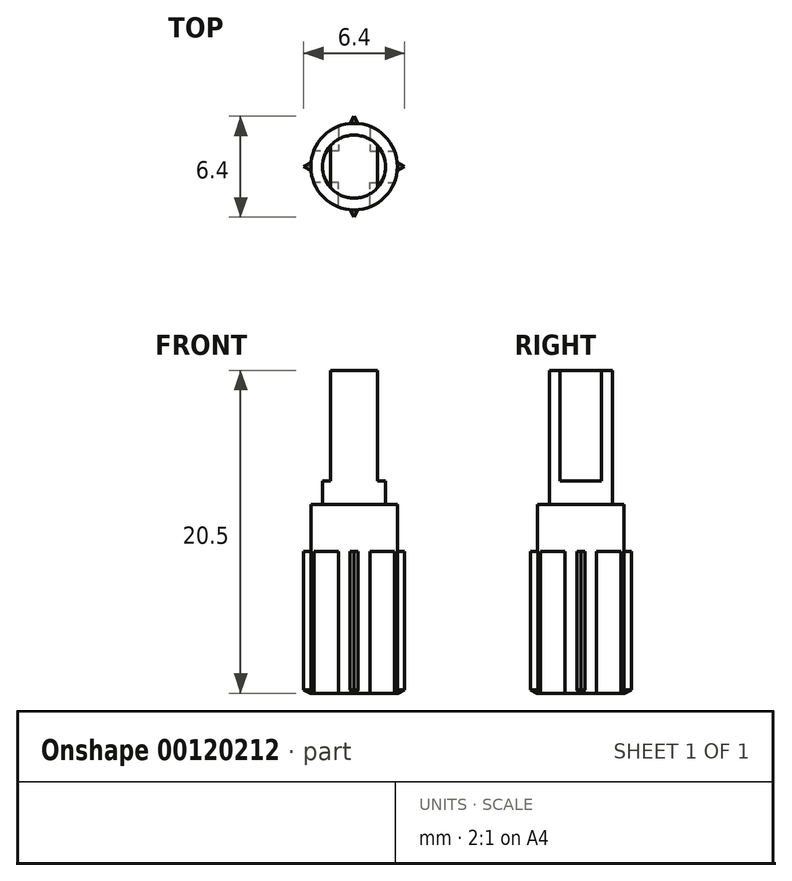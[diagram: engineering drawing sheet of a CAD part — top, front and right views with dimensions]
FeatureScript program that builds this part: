
annotation { "Feature Type Name" : "Feature", "Feature Type Description" : "" }
export const myFeature = defineFeature(function(context is Context, id is Id, definition is map)
    precondition{}
    {
        {
            var Q0;
            Q0=qCreatedBy(makeId("Top.planeOp"),FACE);
            var sketch = newSketch(context, id + "F0", { "sketchPlane" : qUnion([Q0])});
            skCircle(sketch, "E0", {"center": v(0, 0) * mm, "radius": 2.75 * mm});
            skCircle(sketch, "E1", {"center": v(0, 0) * mm, "radius": 2 * mm});
            skSolve(sketch);
        }
        {
            var Q0;
            Q0=makeQuery(id+"F0.imprint","IMPRINT",FACE,{"disambiguationData":[TD([[makeQuery(id+"F0.imprint","IMPRINT",EDGE,{"derivedFrom":sQuery(id+"F0.wireOp",EDGE,"E0")}),1.0]])]});
            var Q1;
            Q1=makeQuery(id+"F0.imprint","IMPRINT",FACE,{"disambiguationData":[TD([[makeQuery(id+"F0.imprint","IMPRINT",EDGE,{"derivedFrom":sQuery(id+"F0.wireOp",EDGE,"E1")}),1.0]])]});
            extrude(context, id + "F1", {"entities" : qUnion([Q0, Q1]), "oppositeDirection" : true, "depth" : 3 * mm});
        }
        {
            var Q0;
            Q0=makeQuery(id+"F0.imprint","IMPRINT",FACE,{"disambiguationData":[TD([[makeQuery(id+"F0.imprint","IMPRINT",EDGE,{"derivedFrom":sQuery(id+"F0.wireOp",EDGE,"E1")}),1.0]])]});
            extrude(context, id + "F2", {"entities" : qUnion([Q0]), "operationType" : NewBodyOperationType.ADD, "depth" : 1.5 * mm});
        }
        {
            var Q0;
            Q0=makeQuery(id+"F2.opExtrude","CAP_FACE",FACE,{"disambiguationData":[OSD([sQuery(id+"F0.wireOp",EDGE,"E1")])],"isStart":false});
            var sketch = newSketch(context, id + "F3", { "sketchPlane" : qUnion([Q0])});
            skLineSegment(sketch, "E2", {"start": v(-1.5, 1.32) * mm, "end": v(-1.5, -1.32) * mm});
            skLineSegment(sketch, "E3", {"start": v(1.5, 1.32) * mm, "end": v(1.5, -1.32) * mm});
            skLineSegment(sketch, "E4", {"start": v(0, 2) * mm, "end": v(0, -2) * mm, "construction": true});
            skSolve(sketch);
        }
        {
            var Q0;
            {var subQ0=sQuery(id+"F3.wireOp",EDGE,"E2");Q0=makeQuery(id+"F3.imprint","IMPRINT",FACE,{"disambiguationData":[TD([[makeQuery(id+"F3.imprint","IMPRINT",EDGE,{"derivedFrom":subQ0}),1.0]])]});}
            extrude(context, id + "F4", {"entities" : qUnion([Q0]), "operationType" : NewBodyOperationType.ADD, "depth" : 7 * mm});
        }
        {
            var Q0;
            Q0=makeQuery(id+"F1.opExtrude","CAP_FACE",FACE,{"disambiguationData":[OSD([sQuery(id+"F0.wireOp",EDGE,"E0")])],"isStart":false});
            var sketch = newSketch(context, id + "F5", { "sketchPlane" : qUnion([Q0])});
            skLineSegment(sketch, "E5", {"start": v(0, -3.52) * mm, "end": v(0, 3.65) * mm, "construction": true});
            skLineSegment(sketch, "E6", {"start": v(3.98, 0) * mm, "end": v(-4.64, 0) * mm, "construction": true});
            skLineSegment(sketch, "E7", {"start": v(1, -2.56) * mm, "end": v(1, -1) * mm});
            skLineSegment(sketch, "E8", {"start": v(1, -1) * mm, "end": v(2.56, -1) * mm});
            skLineSegment(sketch, "E9.MirrorCS", {"start": v(1, 1) * mm, "end": v(2.56, 1) * mm});
            skLineSegment(sketch, "E10.MirrorCS", {"start": v(1, 2.56) * mm, "end": v(1, 1) * mm});
            skLineSegment(sketch, "E11.MirrorCS", {"start": v(-1, -2.56) * mm, "end": v(-1, -1) * mm});
            skLineSegment(sketch, "E12.MirrorCS", {"start": v(-1, -1) * mm, "end": v(-2.56, -1) * mm});
            skLineSegment(sketch, "E13.MirrorCS", {"start": v(-1, 1) * mm, "end": v(-2.56, 1) * mm});
            skLineSegment(sketch, "E14.MirrorCS", {"start": v(-1, 2.56) * mm, "end": v(-1, 1) * mm});
            skLineSegment(sketch, "E15", {"start": v(0, -3.2) * mm, "end": v(0.25, -2.74) * mm});
            skLineSegment(sketch, "E16", {"start": v(0, -3.2) * mm, "end": v(-0.25, -2.74) * mm});
            skLineSegment(sketch, "E17.MirrorCS", {"start": v(0, 3.2) * mm, "end": v(0.25, 2.74) * mm});
            skLineSegment(sketch, "E18.MirrorCS", {"start": v(0, 3.2) * mm, "end": v(-0.25, 2.74) * mm});
            skLineSegment(sketch, "E19", {"start": v(3.2, 0) * mm, "end": v(2.74, 0.25) * mm});
            skLineSegment(sketch, "E20", {"start": v(3.2, 0) * mm, "end": v(2.74, -0.25) * mm});
            skLineSegment(sketch, "E21.MirrorCS", {"start": v(-3.2, 0) * mm, "end": v(-2.74, 0.25) * mm});
            skLineSegment(sketch, "E22.MirrorCS", {"start": v(-3.2, 0) * mm, "end": v(-2.74, -0.25) * mm});
            skSolve(sketch);
        }
        {
            var Q0;
            {var subQ7=sQuery(id+"F5.wireOp",EDGE,"E7");Q0=makeQuery(id+"F5.imprint","IMPRINT",FACE,{"disambiguationData":[TD([[makeQuery(id+"F5.imprint","IMPRINT",EDGE,{"derivedFrom":subQ7}),1.0]])]});}
            var Q1;
            {var subQ0=sQuery(id+"F5.wireOp",EDGE,"E19");Q1=makeQuery(id+"F5.imprint","IMPRINT",FACE,{"disambiguationData":[TD([[makeQuery(id+"F5.imprint","IMPRINT",EDGE,{"derivedFrom":subQ0}),1.0]])]});}
            var Q2;
            {var subQ0=sQuery(id+"F5.wireOp",EDGE,"E15");Q2=makeQuery(id+"F5.imprint","IMPRINT",FACE,{"disambiguationData":[TD([[makeQuery(id+"F5.imprint","IMPRINT",EDGE,{"derivedFrom":subQ0}),1.0]])]});}
            var Q3;
            {var subQ0=sQuery(id+"F5.wireOp",EDGE,"E21.MirrorCS");Q3=makeQuery(id+"F5.imprint","IMPRINT",FACE,{"disambiguationData":[TD([[makeQuery(id+"F5.imprint","IMPRINT",EDGE,{"derivedFrom":subQ0}),-1.0]])]});}
            var Q4;
            {var subQ0=sQuery(id+"F5.wireOp",EDGE,"E17.MirrorCS");Q4=makeQuery(id+"F5.imprint","IMPRINT",FACE,{"disambiguationData":[TD([[makeQuery(id+"F5.imprint","IMPRINT",EDGE,{"derivedFrom":subQ0}),-1.0]])]});}
            extrude(context, id + "F6", {"entities" : qUnion([Q0, Q1, Q2, Q3, Q4]), "operationType" : NewBodyOperationType.ADD, "depth" : 9 * mm});
        }
        {
            var Q0;
            Q0=makeQuery(id+"F6.opExtrude","CAP_EDGE",EDGE,{"disambiguationData":[OSD([sQuery(id+"F5.wireOp",EDGE,"E16")])],"isStart":false});
            var Q1;
            Q1=makeQuery(id+"F6.opExtrude","CAP_EDGE",EDGE,{"disambiguationData":[OSD([sQuery(id+"F5.wireOp",EDGE,"E15")])],"isStart":false});
            var Q2;
            Q2=makeQuery(id+"F6.opExtrude","CAP_EDGE",EDGE,{"disambiguationData":[OSD([sQuery(id+"F5.wireOp",EDGE,"E22.MirrorCS")])],"isStart":false});
            var Q3;
            Q3=makeQuery(id+"F6.opExtrude","CAP_EDGE",EDGE,{"disambiguationData":[OSD([sQuery(id+"F5.wireOp",EDGE,"E21.MirrorCS")])],"isStart":false});
            var Q4;
            Q4=makeQuery(id+"F6.opExtrude","CAP_EDGE",EDGE,{"disambiguationData":[OSD([sQuery(id+"F5.wireOp",EDGE,"E17.MirrorCS")])],"isStart":false});
            var Q5;
            Q5=makeQuery(id+"F6.opExtrude","CAP_EDGE",EDGE,{"disambiguationData":[OSD([sQuery(id+"F5.wireOp",EDGE,"E18.MirrorCS")])],"isStart":false});
            var Q6;
            Q6=makeQuery(id+"F6.opExtrude","CAP_EDGE",EDGE,{"disambiguationData":[OSD([sQuery(id+"F5.wireOp",EDGE,"E19")])],"isStart":false});
            var Q7;
            Q7=makeQuery(id+"F6.opExtrude","CAP_EDGE",EDGE,{"disambiguationData":[OSD([sQuery(id+"F5.wireOp",EDGE,"E20")])],"isStart":false});
            chamfer(context, id + "F7", {"entities" : qUnion([Q0, Q1, Q2, Q3, Q4, Q5, Q6, Q7]), "width" : 0.2 * mm, "tangentPropagation" : true});
        }
    });
